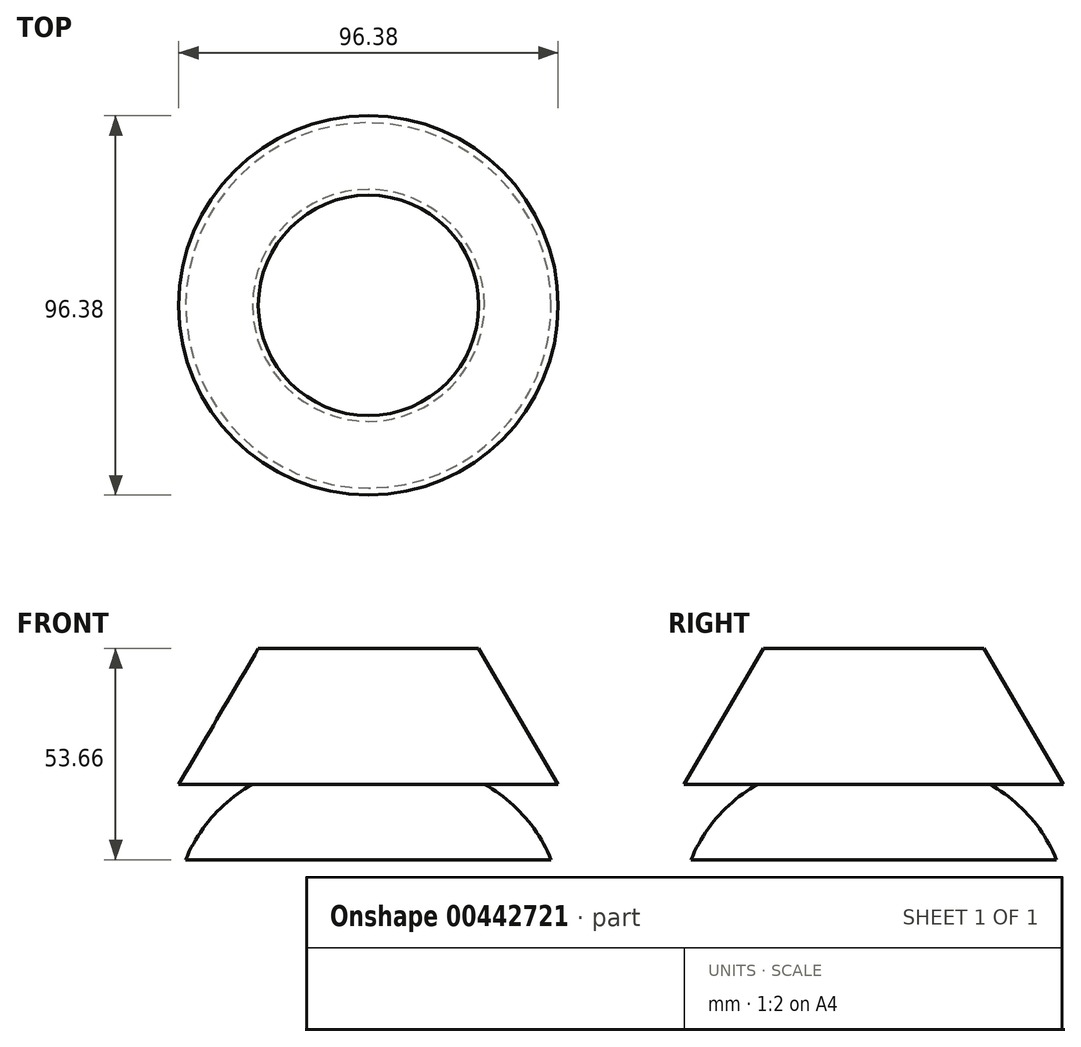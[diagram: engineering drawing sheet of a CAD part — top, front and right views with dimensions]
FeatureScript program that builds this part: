
annotation { "Feature Type Name" : "Feature", "Feature Type Description" : "" }
export const myFeature = defineFeature(function(context is Context, id is Id, definition is map)
    precondition{}
    {
        {
            var Q0;
            Q0=qCreatedBy(makeId("Front.planeOp"),FACE);
            var sketch = newSketch(context, id + "F0", { "sketchPlane" : qUnion([Q0])});
            skLineSegment(sketch, "E0", {"start": v(0, 0) * mm, "end": v(0, 53.66) * mm});
            skLineSegment(sketch, "E1", {"start": v(0, 53.66) * mm, "end": v(-27.99, 53.66) * mm});
            skLineSegment(sketch, "E2", {"start": v(-27.99, 53.66) * mm, "end": v(-48.19, 19.15) * mm});
            skLineSegment(sketch, "E3", {"start": v(-48.19, 19.15) * mm, "end": v(-29.46, 19.15) * mm});
            skArc(sketch, "E4", {"start": v(-29.46, 19.15) * mm, "mid": v(-39.58, 11.02) * mm, "end": v(-46.43, 0) * mm});
            skLineSegment(sketch, "E5", {"start": v(-46.43, 0) * mm, "end": v(0, 0) * mm});
            skSolve(sketch);
        }
        {
            var Q0;
            Q0=makeQuery(id+"F0.imprint","IMPRINT",FACE,{"disambiguationData":[TD([[makeQuery(id+"F0.imprint","IMPRINT",EDGE,{"derivedFrom":sQuery(id+"F0.wireOp",EDGE,"E0")}),1.0]])]});
            var Q1;
            Q1=sQuery(id+"F0.wireOp",EDGE,"E0");
            revolve(context, id + "F1", {"entities" : qUnion([Q0]), "axis" : qUnion([Q1]), "revolveType" : RevolveType.FULL});
        }
    });
